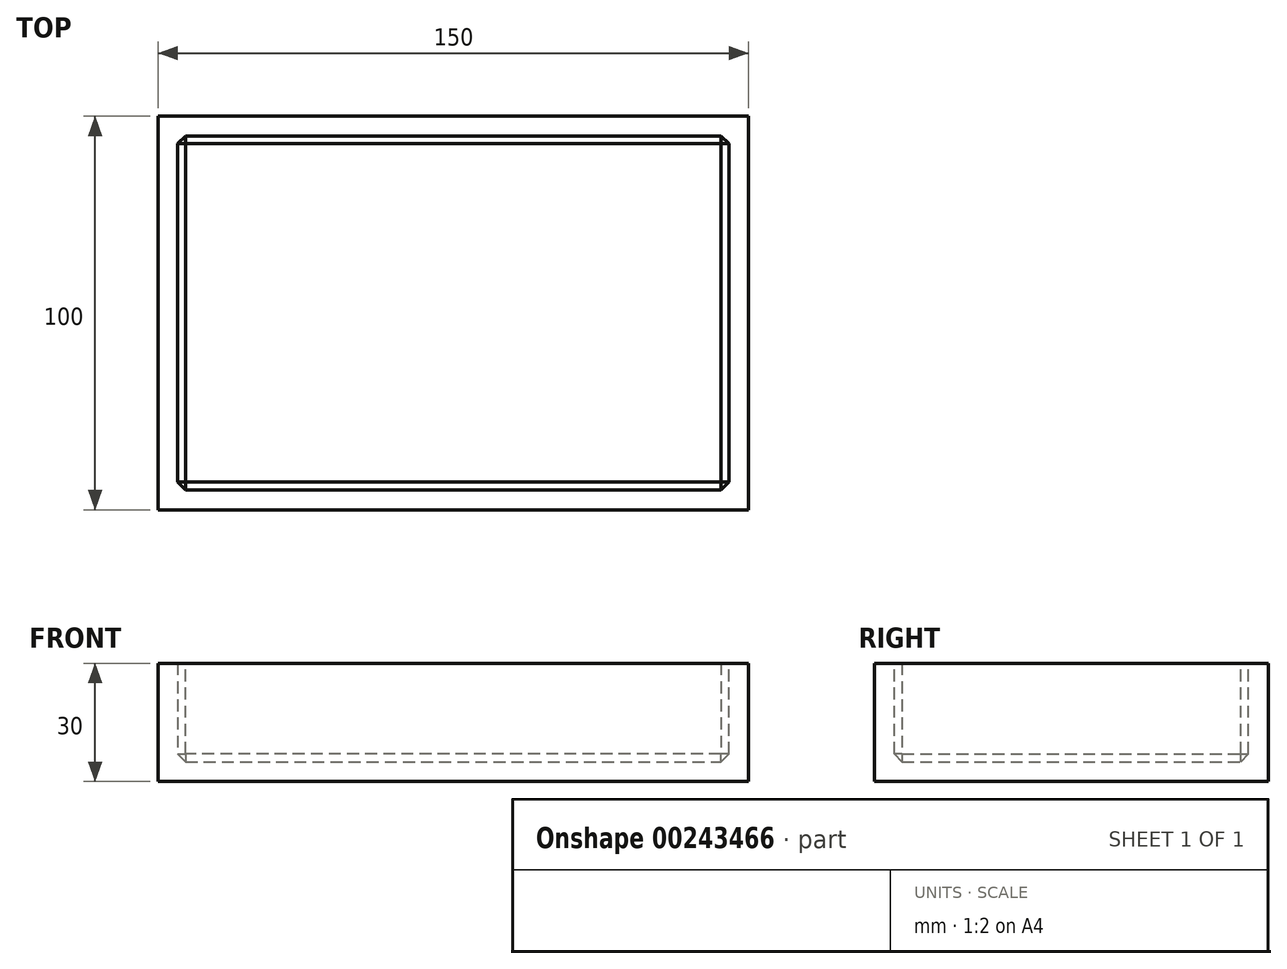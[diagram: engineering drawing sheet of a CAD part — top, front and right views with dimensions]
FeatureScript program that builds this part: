
annotation { "Feature Type Name" : "Feature", "Feature Type Description" : "" }
export const myFeature = defineFeature(function(context is Context, id is Id, definition is map)
    precondition{}
    {
        {
            var Q0;
            Q0=qCreatedBy(makeId("Top.planeOp"),FACE);
            var sketch = newSketch(context, id + "F0", { "sketchPlane" : qUnion([Q0])});
            skLineSegment(sketch, "E0.bottom", {"start": v(75, 50) * mm, "end": v(-75, 50) * mm});
            skLineSegment(sketch, "E0.top", {"start": v(75, -50) * mm, "end": v(-75, -50) * mm});
            skLineSegment(sketch, "E0.left", {"start": v(75, 50) * mm, "end": v(75, -50) * mm});
            skLineSegment(sketch, "E0.right", {"start": v(-75, 50) * mm, "end": v(-75, -50) * mm});
            skPoint(sketch, "E0.middle", {"position": v(0, 0) * mm});
            skSolve(sketch);
        }
        {
            var Q0;
            Q0 = qSketchRegion(id + "F0", true);
            extrude(context, id + "F1", {"entities" : qUnion([Q0]), "depth" : 30 * mm});
        }
        {
            var Q0;
            Q0=makeQuery(id+"F1.opExtrude","CAP_FACE",FACE,{"disambiguationData":[OSD([sQuery(id+"F0.wireOp",EDGE,"E0.bottom"),sQuery(id+"F0.wireOp",EDGE,"E0.top"),sQuery(id+"F0.wireOp",EDGE,"E0.left"),sQuery(id+"F0.wireOp",EDGE,"E0.right")])],"isStart":false});
            var sketch = newSketch(context, id + "F2", { "sketchPlane" : qUnion([Q0])});
            skLineSegment(sketch, "E1.bottom", {"start": v(-70, -45) * mm, "end": v(70, -45) * mm});
            skLineSegment(sketch, "E1.top", {"start": v(-70, 45) * mm, "end": v(70, 45) * mm});
            skLineSegment(sketch, "E1.left", {"start": v(-70, -45) * mm, "end": v(-70, 45) * mm});
            skLineSegment(sketch, "E1.right", {"start": v(70, -45) * mm, "end": v(70, 45) * mm});
            skPoint(sketch, "E1.middle", {"position": v(0, 0) * mm});
            skSolve(sketch);
        }
        {
            var Q0;
            Q0=makeQuery(id+"F2.imprint","IMPRINT",FACE,{"disambiguationData":[TD([[makeQuery(id+"F2.imprint","IMPRINT",EDGE,{"derivedFrom":sQuery(id+"F2.wireOp",EDGE,"E1.bottom")}),1.0]])]});
            extrude(context, id + "F3", {"entities" : qUnion([Q0]), "operationType" : NewBodyOperationType.REMOVE, "oppositeDirection" : true, "depth" : 25 * mm});
        }
        {
            var Q0;
            Q0=makeQuery(id+"F3.boolean.opBoolean","COPY",FACE,{"derivedFrom":makeQuery(id+"F3.opExtrude","CAP_FACE",FACE,{"disambiguationData":[OSD([sQuery(id+"F2.wireOp",EDGE,"E1.bottom"),sQuery(id+"F2.wireOp",EDGE,"E1.top"),sQuery(id+"F2.wireOp",EDGE,"E1.left"),sQuery(id+"F2.wireOp",EDGE,"E1.right")])],"isStart":false})});
            var Q1;
            Q1=makeQuery(id+"F3.boolean.opBoolean","COPY",EDGE,{"derivedFrom":makeQuery(id+"F3.opExtrude","SWEPT_EDGE",EDGE,{"disambiguationData":[OSD([sQuery(id+"F2.wireOp",EDGE,"E1.top"),sQuery(id+"F2.wireOp",EDGE,"E1.left")])]})});
            var Q2;
            Q2=makeQuery(id+"F3.boolean.opBoolean","COPY",EDGE,{"derivedFrom":makeQuery(id+"F3.opExtrude","SWEPT_EDGE",EDGE,{"disambiguationData":[OSD([sQuery(id+"F2.wireOp",EDGE,"E1.top"),sQuery(id+"F2.wireOp",EDGE,"E1.right")])]})});
            var Q3;
            Q3=makeQuery(id+"F3.boolean.opBoolean","COPY",EDGE,{"derivedFrom":makeQuery(id+"F3.opExtrude","SWEPT_EDGE",EDGE,{"disambiguationData":[OSD([sQuery(id+"F2.wireOp",EDGE,"E1.bottom"),sQuery(id+"F2.wireOp",EDGE,"E1.right")])]})});
            var Q4;
            Q4=makeQuery(id+"F3.boolean.opBoolean","COPY",EDGE,{"derivedFrom":makeQuery(id+"F3.opExtrude","SWEPT_EDGE",EDGE,{"disambiguationData":[OSD([sQuery(id+"F2.wireOp",EDGE,"E1.bottom"),sQuery(id+"F2.wireOp",EDGE,"E1.left")])]})});
            chamfer(context, id + "F4", {"entities" : qUnion([Q0, Q1, Q2, Q3, Q4]), "width" : 2 * mm, "tangentPropagation" : true});
        }
    });
